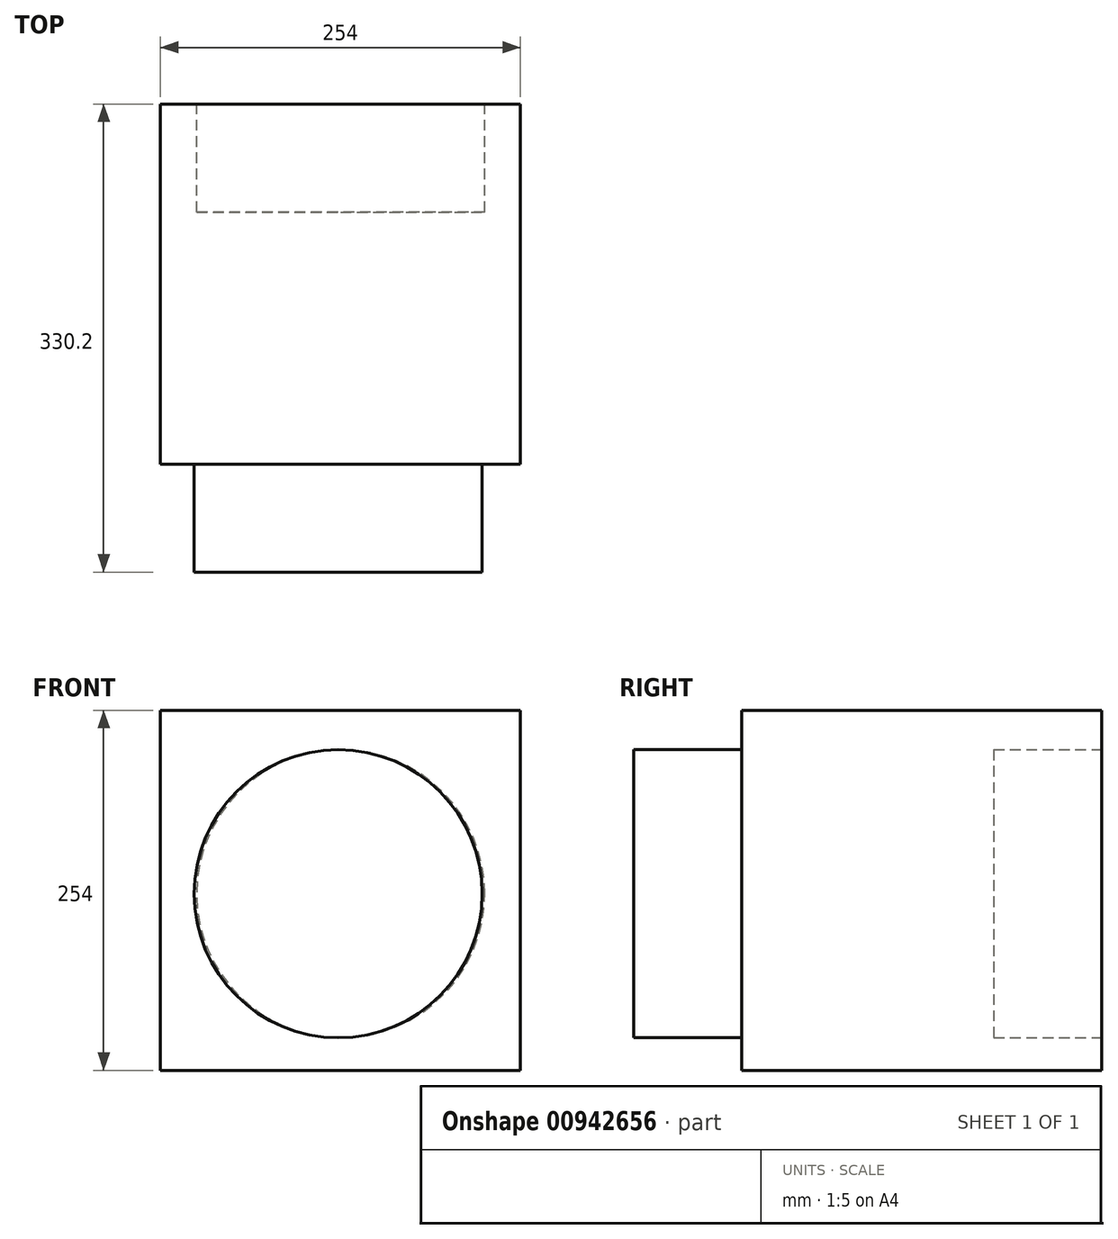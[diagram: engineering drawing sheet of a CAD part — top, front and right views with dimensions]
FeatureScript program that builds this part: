
annotation { "Feature Type Name" : "Feature", "Feature Type Description" : "" }
export const myFeature = defineFeature(function(context is Context, id is Id, definition is map)
    precondition{}
    {
        {
            var Q0;
            Q0=qCreatedBy(makeId("Right.planeOp"),FACE);
            var sketch = newSketch(context, id + "F0", { "sketchPlane" : qUnion([Q0])});
            skLineSegment(sketch, "E0.bottom", {"start": v(-159.03, 129.43) * mm, "end": v(94.97, 129.43) * mm});
            skLineSegment(sketch, "E0.top", {"start": v(-159.03, -124.57) * mm, "end": v(94.97, -124.57) * mm});
            skLineSegment(sketch, "E0.left", {"start": v(-159.03, 129.43) * mm, "end": v(-159.03, -124.57) * mm});
            skLineSegment(sketch, "E0.right", {"start": v(94.97, 129.43) * mm, "end": v(94.97, -124.57) * mm});
            skSolve(sketch);
        }
        {
            var Q0;
            Q0=makeQuery(id+"F0.imprint","IMPRINT",FACE,{"disambiguationData":[TD([[makeQuery(id+"F0.imprint","IMPRINT",EDGE,{"derivedFrom":sQuery(id+"F0.wireOp",EDGE,"E0.bottom")}),-1.0]])]});
            extrude(context, id + "F1", {"entities" : qUnion([Q0]), "oppositeDirection" : true, "depth" : 254 * mm, "offsetDistance" : 25.4 * mm});
        }
        {
            var Q0;
            Q0=makeQuery(id+"F1.opExtrude","SWEPT_FACE",FACE,{"disambiguationData":[OSD([sQuery(id+"F0.wireOp",EDGE,"E0.left")])]});
            var sketch = newSketch(context, id + "F2", { "sketchPlane" : qUnion([Q0])});
            skCircle(sketch, "E1", {"center": v(-128.56, 0) * mm, "radius": 101.6 * mm});
            skSolve(sketch);
        }
        {
            var Q0;
            Q0=makeQuery(id+"F2.imprint","IMPRINT",FACE,{"disambiguationData":[TD([[makeQuery(id+"F2.imprint","IMPRINT",EDGE,{"derivedFrom":sQuery(id+"F2.wireOp",EDGE,"E1")}),1.0]])]});
            extrude(context, id + "F3", {"entities" : qUnion([Q0]), "operationType" : NewBodyOperationType.ADD, "depth" : 76.2 * mm, "offsetDistance" : 25.4 * mm});
        }
        {
            var Q0;
            Q0=makeQuery(id+"F1.opExtrude","SWEPT_FACE",FACE,{"disambiguationData":[OSD([sQuery(id+"F0.wireOp",EDGE,"E0.right")])]});
            var sketch = newSketch(context, id + "F4", { "sketchPlane" : qUnion([Q0])});
            skCircle(sketch, "E2", {"center": v(126.84, 0) * mm, "radius": 101.6 * mm});
            skSolve(sketch);
        }
        {
            var Q0;
            Q0=makeQuery(id+"F4.imprint","IMPRINT",FACE,{"disambiguationData":[TD([[makeQuery(id+"F4.imprint","IMPRINT",EDGE,{"derivedFrom":sQuery(id+"F4.wireOp",EDGE,"E2")}),1.0]])]});
            var Q1;
            Q1=sQuery(id+"F4.wireOp",EDGE,"E2");
            extrude(context, id + "F5", {"entities" : qUnion([Q0]), "operationType" : NewBodyOperationType.REMOVE, "surfaceEntities" : qUnion([Q1]), "oppositeDirection" : true, "depth" : 76.2 * mm, "offsetDistance" : 25.4 * mm});
        }
    });
